# Revit family: 05111_KR
name_source: partatom
category: Air Terminals
revit_build: Autodesk Revit MEP 2012 (Build: 20110309_2315(x64)
units: mm (PartAtom-declared; Revit-internal decimal feet)

## types (8) — shared parameters
Description = Difusor de Largo alcance
Manufacturer = INNES
Material = Aluminio
Model = KR
Nota1 = .
Posición de Instalación = Muro/Techo
Tipo de Cuello = Redondo
Type Comments = Tipo tobera
URL = https://www.innes.com.mx
Visible_Texto = No

## per-type parameters (varying)
| type | Conect | Cuello Mín-Máx. | Función | Tamanio_Requerido | Var |
| KR-06 | 3.38 " | 6 a 20" en incrementos de 2". | Inyeccion | 6 | 6 |
| KR-08 | 4.25 " | 6 a 20" en incrementos de 2". | Inyeccion | 8 | 8 |
| KR-10 | 5.4 " | 6 a 20" en incrementos de 2". | Inyeccion | 10 | 10 |
| KR-12 | 6.17 " | 6 a 20" en incrementos de 2". | Inyeccion | 12 | 12 |
| KR-14 | 6.09 " | 6 a 20" en incrementos de 2". | Inyeccion | 14 | 14 |
| KR-16 | 8.7 " | 6 a 20" en incrementos de 2". | Inyeccion | 16 | 16 |
| KR-18 | 9.4 " | 6 a 20" en incrementos de 2". | Inyeccion | 18 | 18 |
| KR-20 | 9.37 " | 6" a 20" en incrementos de 2" | Inyección | 20 | 20 |

## geometry (parser evidence)
native form markers: Sweep x8
no freeform markers — native parametric forms only
